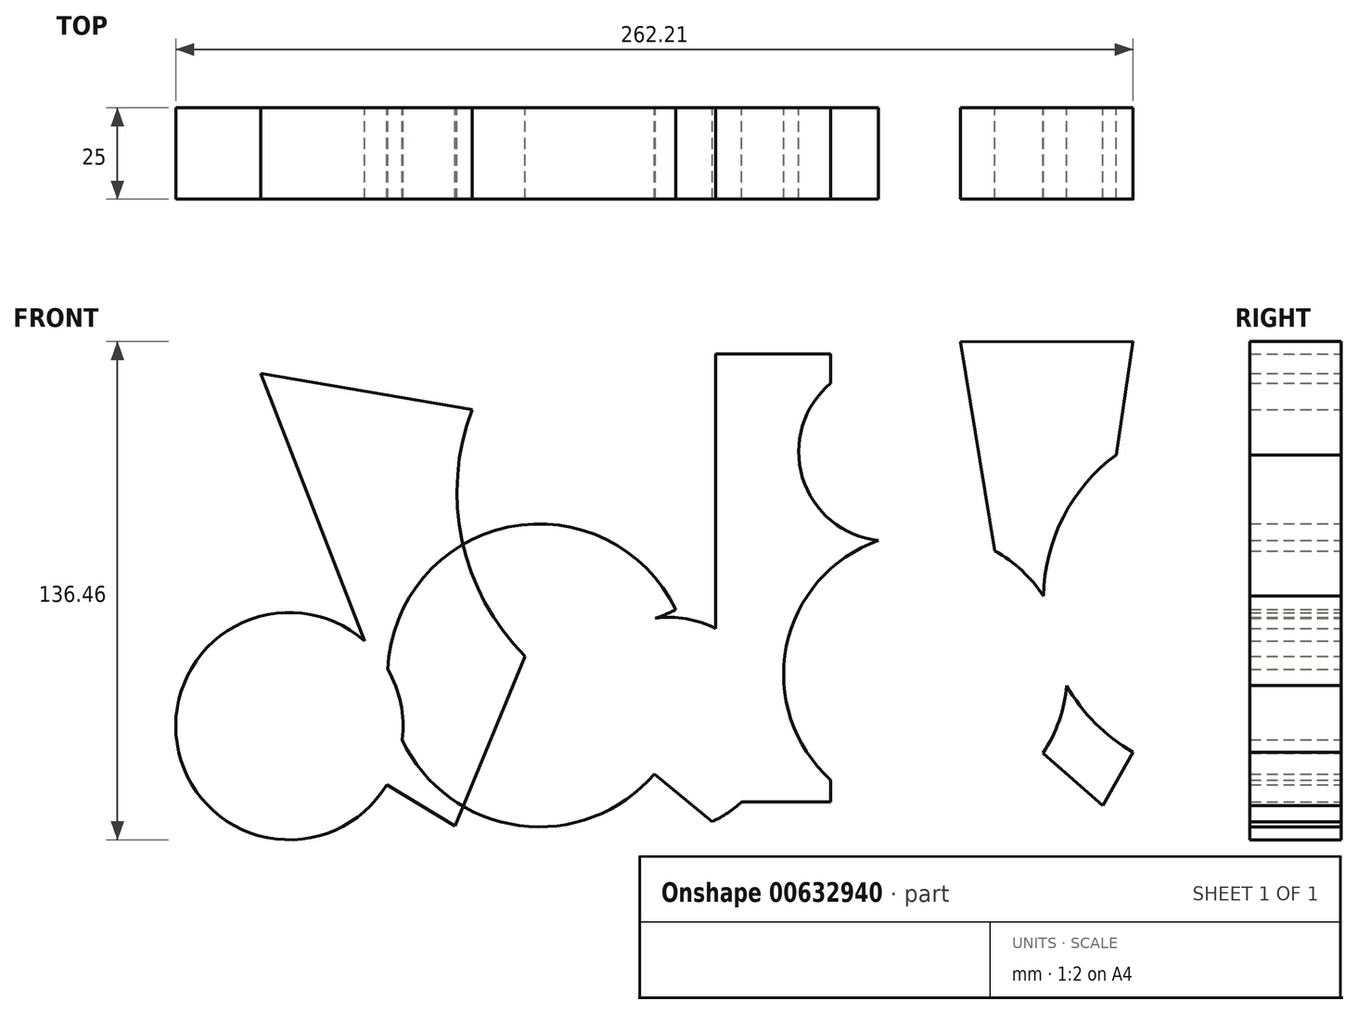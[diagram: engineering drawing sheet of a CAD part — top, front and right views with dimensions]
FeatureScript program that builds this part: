
annotation { "Feature Type Name" : "Feature", "Feature Type Description" : "" }
export const myFeature = defineFeature(function(context is Context, id is Id, definition is map)
    precondition{}
    {
        {
            var Q0;
            Q0=qCreatedBy(makeId("Front.planeOp"),FACE);
            var sketch = newSketch(context, id + "F0", { "sketchPlane" : qUnion([Q0])});
            skCircle(sketch, "E0", {"center": v(-84.16, 0) * mm, "radius": 31.13 * mm});
            skLineSegment(sketch, "E1", {"start": v(-63.56, 23.33) * mm, "end": v(-92.07, 96.58) * mm});
            skLineSegment(sketch, "E2", {"start": v(-92.07, 96.58) * mm, "end": v(-34.1, 86.71) * mm});
            skLineSegment(sketch, "E3", {"start": v(-34.1, 86.71) * mm, "end": v(-34.1, 86.71) * mm});
            skArc(sketch, "E4", {"start": v(-34.1, 86.71) * mm, "mid": v(-36.84, 50.8) * mm, "end": v(-19.64, 19.15) * mm});
            skLineSegment(sketch, "E5", {"start": v(-19.64, 19.15) * mm, "end": v(-38.82, -27.37) * mm});
            skLineSegment(sketch, "E6", {"start": v(-38.82, -27.37) * mm, "end": v(-84.16, 0) * mm});
            skCircle(sketch, "E7", {"center": v(-21.98, 72.15) * mm, "radius": 24.9 * mm});
            skLineSegment(sketch, "E8", {"start": v(0, 83.85) * mm, "end": v(0, 99.72) * mm});
            skArc(sketch, "E9", {"start": v(18.92, 30.9) * mm, "mid": v(27.8, 33.99) * mm, "end": v(36.2, 38.22) * mm});
            skSolve(sketch);
        }
        {
            var Q0;
            Q0 = qSketchRegion(id + "F0", true);
            var sketch = newSketch(context, id + "F1", { "sketchPlane" : qUnion([Q0])});
            skArc(sketch, "E10", {"start": v(16.11, 29.6) * mm, "mid": v(40.33, 72.07) * mm, "end": v(0, 99.7) * mm});
            skArc(sketch, "E11", {"start": v(31.65, -26.15) * mm, "mid": v(47.79, 8.39) * mm, "end": v(16.11, 29.6) * mm});
            skLineSegment(sketch, "E12", {"start": v(31.65, -26.15) * mm, "end": v(0, 0) * mm});
            skCircle(sketch, "E13", {"center": v(-15.72, 13.9) * mm, "radius": 41.5 * mm});
            skLineSegment(sketch, "E14.bottom", {"start": v(32.57, 101.9) * mm, "end": v(64.14, 101.9) * mm});
            skLineSegment(sketch, "E14.top", {"start": v(32.57, -20.71) * mm, "end": v(64.14, -20.71) * mm});
            skLineSegment(sketch, "E14.left", {"start": v(32.57, 101.9) * mm, "end": v(32.57, -20.71) * mm});
            skLineSegment(sketch, "E14.right", {"start": v(64.14, 101.9) * mm, "end": v(64.14, -20.71) * mm});
            skCircle(sketch, "E15", {"center": v(79.81, 75.17) * mm, "radius": 24.48 * mm});
            skCircle(sketch, "E16", {"center": v(90, 14.2) * mm, "radius": 38.81 * mm});
            skLineSegment(sketch, "E17", {"start": v(109.08, 48) * mm, "end": v(99.67, 105.26) * mm});
            skLineSegment(sketch, "E18", {"start": v(99.67, 105.26) * mm, "end": v(146.83, 105.33) * mm});
            skLineSegment(sketch, "E19", {"start": v(146.83, 105.33) * mm, "end": v(135.58, 28.29) * mm});
            skCircle(sketch, "E20", {"center": v(171, 35.08) * mm, "radius": 48.6 * mm});
            skLineSegment(sketch, "E21", {"start": v(113.82, 0) * mm, "end": v(138.69, -21.77) * mm});
            skLineSegment(sketch, "E22", {"start": v(138.69, -21.77) * mm, "end": v(163.49, 22.24) * mm});
            skSolve(sketch);
        }
        {
            var Q0;
            Q0=qCreatedBy(makeId("Front.planeOp"),FACE);
            var sketch = newSketch(context, id + "F2", { "sketchPlane" : qUnion([Q0])});
            skLineSegment(sketch, "E23", {"start": v(0, 84.71) * mm, "end": v(-10.15, 36.62) * mm});
            skLineSegment(sketch, "E24", {"start": v(-10.15, 36.62) * mm, "end": v(19.45, 30.44) * mm});
            skSolve(sketch);
        }
        {
            var Q0;
            Q0 = qSketchRegion(id + "F2", true);
            var Q1;
            {var subQ0=sQuery(id+"F0.wireOp",EDGE,"E0");var subQ1=makeQuery(id+"F0.imprint","INTERSECT",VERTEX,{"derivedFrom":[subQ0,sQuery(id+"F0.wireOp",EDGE,"E1")]});Q1=makeQuery(id+"F0.imprint","IMPRINT",FACE,{"disambiguationData":[TD([[makeQuery(id+"F0.imprint","IMPRINT",EDGE,{"disambiguationData":[TD([[subQ1,-1.0]])],"derivedFrom":subQ0}),1.0]])]});}
            var Q2;
            {var subQ0=sQuery(id+"F0.wireOp",EDGE,"E5");var subQ1=makeQuery(id+"F0.imprint","IMPRINT",EDGE,{"derivedFrom":subQ0});var subQ5=sQuery(id+"F1.wireOp",EDGE,"E13");var subQ7=makeQuery(id+"F1.imprint","INTERSECT",VERTEX,{"derivedFrom":[subQ1,subQ5]});Q2=makeQuery(id+"F1.imprint","IMPRINT",FACE,{"disambiguationData":[TD([[makeQuery(id+"F1.imprint","IMPRINT",EDGE,{"disambiguationData":[TD([[subQ7,1.0]])],"derivedFrom":subQ5}),1.0]])]});}
            var Q3;
            {var subQ0=sQuery(id+"F0.wireOp",EDGE,"E7");var subQ1=makeQuery(id+"F0.imprint","IMPRINT",VERTEX,{"derivedFrom":subQ0});var subQ4=makeQuery(id+"F0.imprint","IMPRINT",EDGE,{"disambiguationData":[TD([[subQ1,-1.0]])],"derivedFrom":subQ0});Q3=makeQuery(id+"F1.imprint","IMPRINT",FACE,{"disambiguationData":[TD([[makeQuery(id+"F1.imprint","IMPRINT",EDGE,{"derivedFrom":subQ4}),1.0]])]});}
            var Q4;
            {var subQ0=sQuery(id+"F1.wireOp",EDGE,"E14.top");var subQ1=sQuery(id+"F1.wireOp",EDGE,"E11");var subQ2=makeQuery(id+"F1.imprint","INTERSECT",VERTEX,{"derivedFrom":[subQ1,subQ0]});Q4=makeQuery(id+"F1.imprint","IMPRINT",FACE,{"disambiguationData":[TD([[makeQuery(id+"F1.imprint","IMPRINT",EDGE,{"disambiguationData":[TD([[subQ2,-1.0]])],"derivedFrom":subQ1}),1.0]])]});}
            var Q5;
            {var subQ1=sQuery(id+"F1.wireOp",EDGE,"E12");var subQ3=sQuery(id+"F1.wireOp",EDGE,"E11");var subQ7=makeQuery(id+"F1.imprint","INTERSECT",VERTEX,{"derivedFrom":[subQ3,subQ1]});Q5=makeQuery(id+"F1.imprint","IMPRINT",FACE,{"disambiguationData":[TD([[makeQuery(id+"F1.imprint","IMPRINT",EDGE,{"disambiguationData":[TD([[subQ7,-1.0]])],"derivedFrom":subQ3}),1.0]])]});}
            var Q6;
            {var subQ1=sQuery(id+"F1.wireOp",EDGE,"E10");var subQ12=sQuery(id+"F1.wireOp",EDGE,"E11");var subQ13=makeQuery(id+"F1.imprint","INTERSECT",VERTEX,{"derivedFrom":[subQ1,subQ12]});Q6=makeQuery(id+"F1.imprint","IMPRINT",FACE,{"disambiguationData":[TD([[makeQuery(id+"F1.imprint","IMPRINT",EDGE,{"disambiguationData":[TD([[subQ13,-1.0]])],"derivedFrom":subQ1}),1.0]])]});}
            var Q7;
            {var subQ0=sQuery(id+"F1.wireOp",EDGE,"E20");var subQ1=sQuery(id+"F1.wireOp",EDGE,"E16");var subQ2=makeQuery(id+"F1.imprint","INTERSECT",VERTEX,{"disambiguationData":[OD(0.0)],"derivedFrom":[subQ1,subQ0]});Q7=makeQuery(id+"F1.imprint","IMPRINT",FACE,{"disambiguationData":[TD([[makeQuery(id+"F1.imprint","IMPRINT",EDGE,{"disambiguationData":[TD([[subQ2,1.0]])],"derivedFrom":subQ1}),-1.0]])]});}
            var Q8;
            {var subQ0=sQuery(id+"F1.wireOp",EDGE,"E21");var subQ1=sQuery(id+"F1.wireOp",EDGE,"E16");var subQ2=makeQuery(id+"F1.imprint","INTERSECT",VERTEX,{"derivedFrom":[subQ1,subQ0]});Q8=makeQuery(id+"F1.imprint","IMPRINT",FACE,{"disambiguationData":[TD([[makeQuery(id+"F1.imprint","IMPRINT",EDGE,{"disambiguationData":[TD([[subQ2,-1.0]])],"derivedFrom":subQ1}),-1.0]])]});}
            var Q9;
            {var subQ0=sQuery(id+"F1.wireOp",EDGE,"E18");Q9=makeQuery(id+"F1.imprint","IMPRINT",FACE,{"disambiguationData":[TD([[makeQuery(id+"F1.imprint","IMPRINT",EDGE,{"derivedFrom":subQ0}),-1.0]])]});}
            var Q10;
            {var subQ0=sQuery(id+"F0.wireOp",EDGE,"E4");var subQ1=sQuery(id+"F0.wireOp",EDGE,"E2");var subQ2=makeQuery(id+"F0.imprint","INTERSECT",VERTEX,{"derivedFrom":[subQ1,subQ0]});Q10=makeQuery(id+"F0.imprint","IMPRINT",FACE,{"disambiguationData":[TD([[makeQuery(id+"F0.imprint","IMPRINT",EDGE,{"disambiguationData":[TD([[subQ2,1.0]])],"derivedFrom":subQ1}),-1.0]])]});}
            var Q11;
            {var subQ1=sQuery(id+"F0.wireOp",EDGE,"E1");Q11=makeQuery(id+"F0.imprint","IMPRINT",FACE,{"disambiguationData":[TD([[makeQuery(id+"F0.imprint","IMPRINT",EDGE,{"derivedFrom":subQ1}),-1.0]])]});}
            var Q12;
            {var subQ0=sQuery(id+"F1.wireOp",EDGE,"E14.left");var subQ1=sQuery(id+"F1.wireOp",EDGE,"E10");var subQ2=makeQuery(id+"F1.imprint","INTERSECT",VERTEX,{"disambiguationData":[OD(0.0)],"derivedFrom":[subQ1,subQ0]});Q12=makeQuery(id+"F1.imprint","IMPRINT",FACE,{"disambiguationData":[TD([[makeQuery(id+"F1.imprint","IMPRINT",EDGE,{"disambiguationData":[TD([[subQ2,1.0]])],"derivedFrom":subQ1}),1.0]])]});}
            var Q13;
            {var subQ0=sQuery(id+"F1.wireOp",EDGE,"E16");var subQ1=sQuery(id+"F1.wireOp",EDGE,"E14.right");var subQ2=makeQuery(id+"F1.imprint","INTERSECT",VERTEX,{"disambiguationData":[OD(0.0)],"derivedFrom":[subQ1,subQ0]});Q13=makeQuery(id+"F1.imprint","IMPRINT",FACE,{"disambiguationData":[TD([[makeQuery(id+"F1.imprint","IMPRINT",EDGE,{"disambiguationData":[TD([[subQ2,1.0]])],"derivedFrom":subQ1}),-1.0]])]});}
            var Q14;
            {var subQ0=sQuery(id+"F1.wireOp",EDGE,"E15");var subQ1=sQuery(id+"F1.wireOp",EDGE,"E14.right");var subQ2=makeQuery(id+"F1.imprint","INTERSECT",VERTEX,{"disambiguationData":[OD(1.0)],"derivedFrom":[subQ1,subQ0]});Q14=makeQuery(id+"F1.imprint","IMPRINT",FACE,{"disambiguationData":[TD([[makeQuery(id+"F1.imprint","IMPRINT",EDGE,{"disambiguationData":[TD([[subQ2,-1.0]])],"derivedFrom":subQ1}),1.0]])]});}
            var Q15;
            {var subQ0=sQuery(id+"F1.wireOp",EDGE,"E16");var subQ7=sQuery(id+"F1.wireOp",EDGE,"E14.right");var subQ8=makeQuery(id+"F1.imprint","INTERSECT",VERTEX,{"disambiguationData":[OD(0.0)],"derivedFrom":[subQ7,subQ0]});Q15=makeQuery(id+"F1.imprint","IMPRINT",FACE,{"disambiguationData":[TD([[makeQuery(id+"F1.imprint","IMPRINT",EDGE,{"disambiguationData":[TD([[subQ8,1.0]])],"derivedFrom":subQ7}),1.0]])]});}
            var Q16;
            {var subQ5=sQuery(id+"F1.wireOp",EDGE,"E14.bottom");Q16=makeQuery(id+"F1.imprint","IMPRINT",FACE,{"disambiguationData":[TD([[makeQuery(id+"F1.imprint","IMPRINT",EDGE,{"derivedFrom":subQ5}),-1.0]])]});}
            extrude(context, id + "F3", {"entities" : qUnion([Q0, Q1, Q2, Q3, Q4, Q5, Q6, Q7, Q8, Q9, Q10, Q11, Q12, Q13, Q14, Q15, Q16]), "depth" : 25 * mm, "offsetDistance" : 25 * mm});
        }
    });
